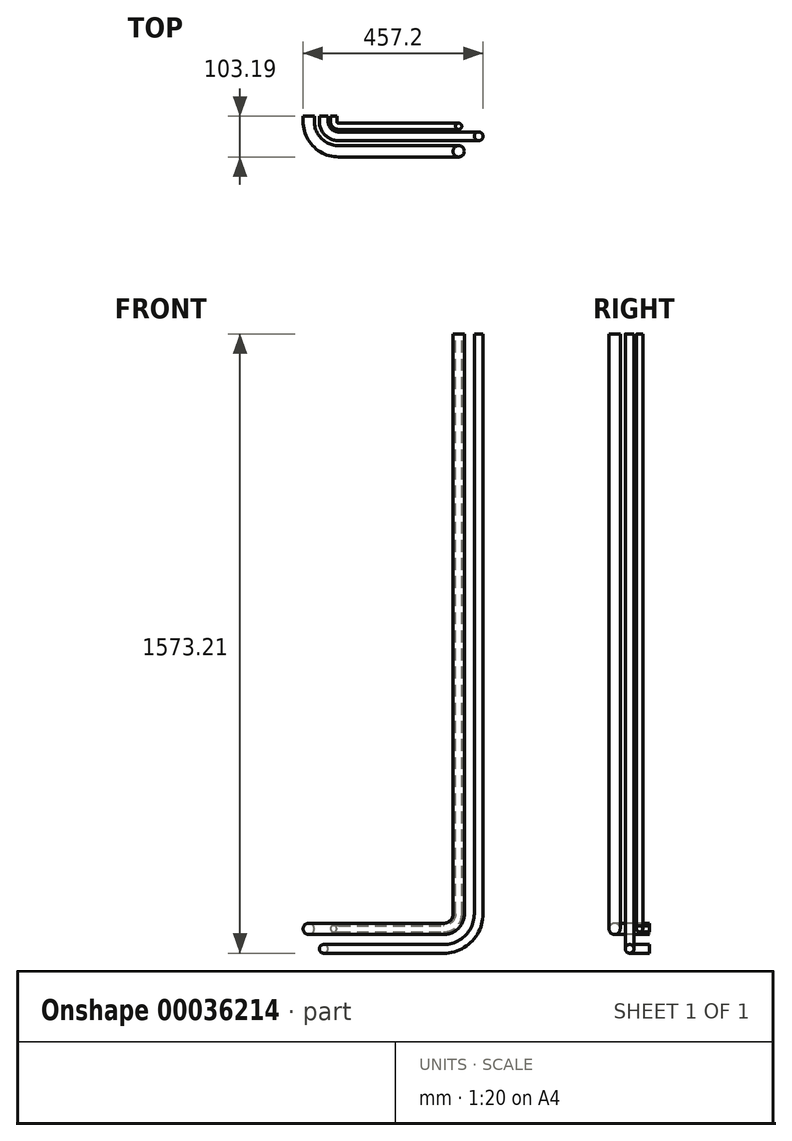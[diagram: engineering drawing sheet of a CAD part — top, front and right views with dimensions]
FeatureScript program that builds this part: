
annotation { "Feature Type Name" : "Feature", "Feature Type Description" : "" }
export const myFeature = defineFeature(function(context is Context, id is Id, definition is map)
    precondition{}
    {
        {
            var Q0;
            Q0=qCreatedBy(makeId("Front.planeOp"),FACE);
            var sketch = newSketch(context, id + "F0", { "sketchPlane" : qUnion([Q0])});
            skCircle(sketch, "E0", {"center": v(-38.1, 50.8) * mm, "radius": 14.29 * mm});
            skCircle(sketch, "E1", {"center": v(25.4, 50.8) * mm, "radius": 7.94 * mm});
            skCircle(sketch, "E2", {"center": v(0, 0) * mm, "radius": 11.11 * mm});
            skLineSegment(sketch, "E3", {"start": v(-38.1, 50.8) * mm, "end": v(25.4, 50.8) * mm, "construction": true});
            skSolve(sketch);
        }
        {
            var Q0;
            Q0=qCreatedBy(makeId("Top.planeOp"),FACE);
            var sketch = newSketch(context, id + "F1", { "sketchPlane" : qUnion([Q0])});
            skLineSegment(sketch, "E4", {"start": v(0, -12.7) * mm, "end": v(0, 0) * mm});
            skLineSegment(sketch, "E5", {"start": v(38.1, -50.8) * mm, "end": v(304.8, -50.8) * mm});
            skPoint(sketch, "E6.visualSharp", {"position": v(0, -50.8) * mm});
            skArc(sketch, "E6.filletArc", {"start": v(0, -12.7) * mm, "mid": v(11.16, -39.64) * mm, "end": v(38.1, -50.8) * mm});
            skSolve(sketch);
        }
        {
            var Q0;
            Q0=makeQuery(id+"F0.imprint","IMPRINT",FACE,{"disambiguationData":[TD([[makeQuery(id+"F0.imprint","IMPRINT",EDGE,{"derivedFrom":sQuery(id+"F0.wireOp",EDGE,"E2")}),1.0]])]});
            var Q1;
            Q1=makeQuery(id+"F0.imprint","IMPRINT",FACE,{"disambiguationData":[TD([[makeQuery(id+"F0.imprint","IMPRINT",EDGE,{"derivedFrom":sQuery(id+"F0.wireOp",EDGE,"E1")}),1.0]])]});
            var Q2;
            Q2=makeQuery(id+"F0.imprint","IMPRINT",FACE,{"disambiguationData":[TD([[makeQuery(id+"F0.imprint","IMPRINT",EDGE,{"derivedFrom":sQuery(id+"F0.wireOp",EDGE,"E0")}),1.0]])]});
            var Q3;
            Q3=sQuery(id+"F1.wireOp",EDGE,"E4");
            var Q4;
            Q4=sQuery(id+"F1.wireOp",EDGE,"E6.filletArc");
            var Q5;
            Q5=sQuery(id+"F1.wireOp",EDGE,"E5");
            sweep(context, id + "F2", {"profiles" : qUnion([Q0, Q1, Q2]), "path" : qUnion([Q3, Q4, Q5])});
        }
        {
            var Q0;
            Q0=qCreatedBy(makeId("Front.planeOp"),FACE);
            var Q1;
            Q1=sQuery(id+"F1.wireOp",VERTEX,"E5.end");
            cPlane(context, id + "F3", {"entities" : qUnion([Q0, Q1]), "cplaneType" : CPlaneType.PLANE_POINT, "offset" : 152.4 * mm, "width" : 152.4 * mm, "height" : 152.4 * mm});
        }
        {
            var Q0;
            Q0=qCreatedBy(id+"F3.planeOp",FACE);
            var sketch = newSketch(context, id + "F4", { "sketchPlane" : qUnion([Q0])});
            skArc(sketch, "E7", {"start": v(304.8, 50.8) * mm, "mid": v(331.74, 61.96) * mm, "end": v(342.9, 88.9) * mm});
            skLineSegment(sketch, "E8", {"start": v(342.9, 88.9) * mm, "end": v(342.9, 1562.1) * mm});
            skSolve(sketch);
        }
        {
            var Q0;
            Q0=makeQuery(id+"F2.opSweep","CAP_FACE",FACE,{"disambiguationData":[OSD([sQuery(id+"F0.wireOp",EDGE,"E1"),sQuery(id+"F1.wireOp",VERTEX,"E5.end")])],"isStart":false});
            var Q1;
            Q1=makeQuery(id+"F2.opSweep","CAP_FACE",FACE,{"disambiguationData":[OSD([sQuery(id+"F0.wireOp",EDGE,"E0"),sQuery(id+"F1.wireOp",VERTEX,"E5.end")])],"isStart":false});
            var Q2;
            Q2=makeQuery(id+"F2.opSweep","CAP_FACE",FACE,{"disambiguationData":[OSD([sQuery(id+"F0.wireOp",EDGE,"E2"),sQuery(id+"F1.wireOp",VERTEX,"E5.end")])],"isStart":false});
            var Q3;
            Q3=sQuery(id+"F4.wireOp",EDGE,"E7");
            var Q4;
            Q4=sQuery(id+"F4.wireOp",EDGE,"E8");
            sweep(context, id + "F5", {"operationType" : NewBodyOperationType.ADD, "profiles" : qUnion([Q0, Q1, Q2]), "path" : qUnion([Q3, Q4])});
        }
    });
